# Revit family: Haworth_Hobo_Sofas_ArmlesswithBench
name_source: partatom
category: Furniture
revit_build: Autodesk Revit 2018 (Build: 20170223_1515(x64)
units: mm (PartAtom-declared; Revit-internal decimal feet)

## family parameters
Always vertical = Yes
Cut with Voids When Loaded = No
OmniClass Number = 23.40.70.14.64.21
OmniClass Title = Systems Furniture
Room Calculation Point = No
Shared = No
Work Plane-Based = No

## types (2) — shared parameters
Actual Depth = 33 1/2"
Actual Height = 28 3/4"
Assembly Code = E2020200
Leg Offset = 4 235/256"
Manufacturer = Haworth
Model = HCCE-HBL
Revision Number = 1
Size = Verify Final Dim. w/ Haworth
URL = http://www.haworth.com
URL - Product = https://www.haworth.com
Warranty = http://www.haworth.com

## per-type parameters (varying)
| type | Actual Width | Description | One Seat | Seat Width | Two Seats |
| HCCE-HBL2 - Two Seats Sofa Armless with Bench | 94 1/2" | Haworth Hobo Two Seats Sofa Armless with Bench | No | 94 1/2" | Yes |
| HCCE-HBL1 - One Seat Sofa Armless with Bench | 63" | Haworth Hobo One Seat Sofa Armless with Bench | Yes | 63" | No |

## geometry (parser evidence)
native form markers: Extrusion x2, Sweep x6
no freeform markers — native parametric forms only
